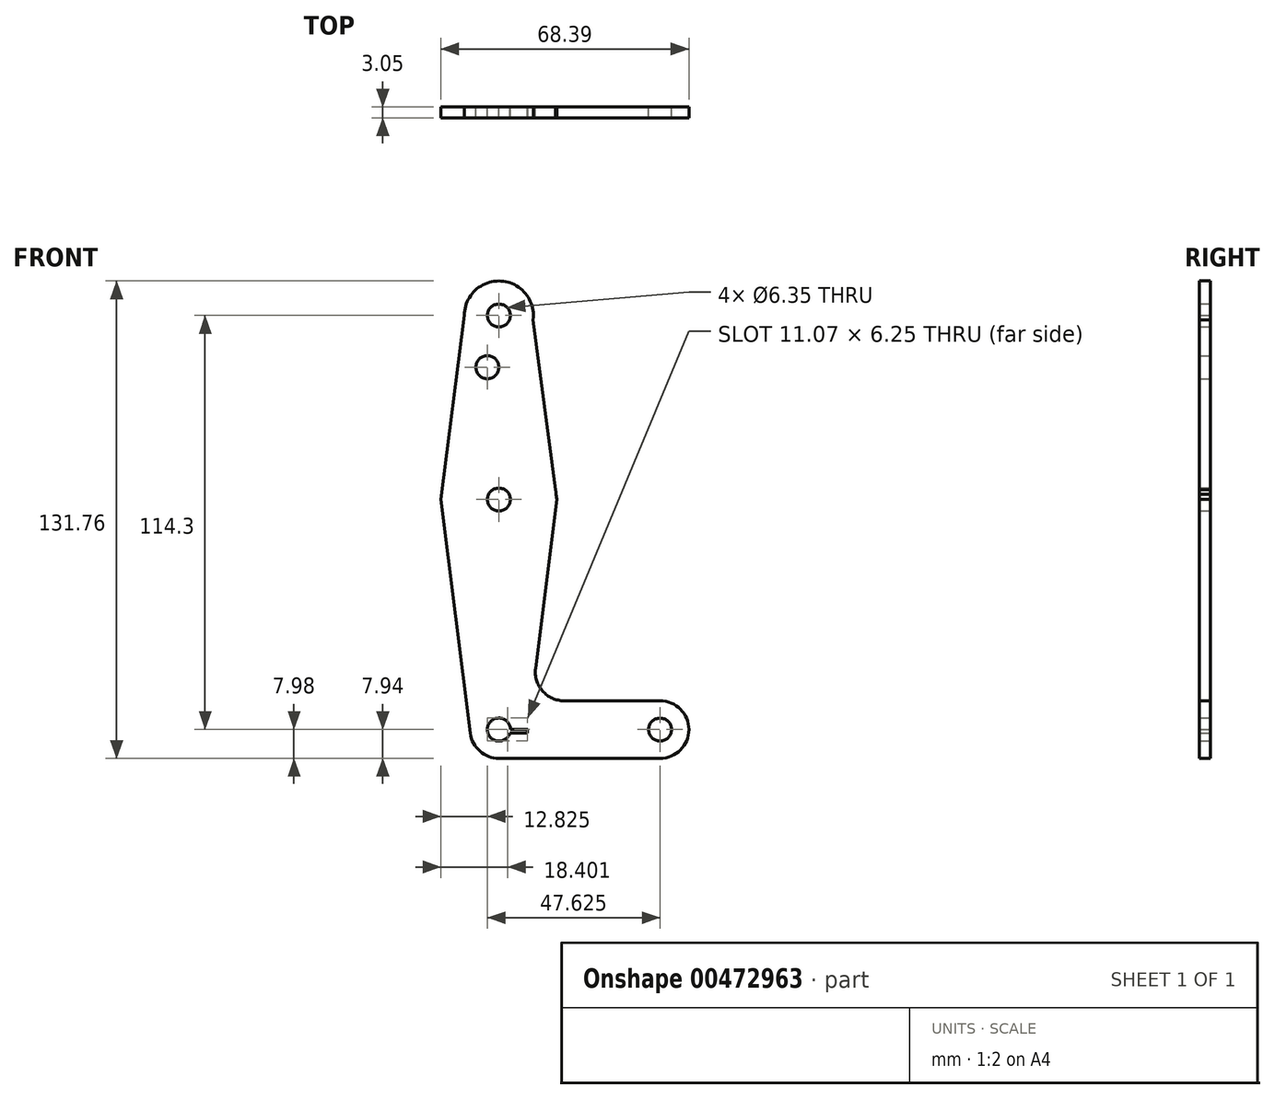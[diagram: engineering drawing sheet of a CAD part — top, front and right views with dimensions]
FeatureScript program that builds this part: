
annotation { "Feature Type Name" : "Feature", "Feature Type Description" : "" }
export const myFeature = defineFeature(function(context is Context, id is Id, definition is map)
    precondition{}
    {
        {
            var Q0;
            Q0=qCreatedBy(makeId("Front.planeOp"),FACE);
            var sketch = newSketch(context, id + "F0", { "sketchPlane" : qUnion([Q0])});
            skLineSegment(sketch, "E0", {"start": v(0, 50.8) * mm, "end": v(0, 0) * mm});
            skLineSegment(sketch, "E1", {"start": v(0, -63.5) * mm, "end": v(0, 0) * mm});
            skLineSegment(sketch, "E2", {"start": v(0, -63.5) * mm, "end": v(44.45, -63.5) * mm});
            skCircle(sketch, "E3", {"center": v(44.45, -63.5) * mm, "radius": 7.94 * mm});
            skCircle(sketch, "E4", {"center": v(0, -63.5) * mm, "radius": 7.94 * mm});
            skCircle(sketch, "E5", {"center": v(0, 0) * mm, "radius": 15.88 * mm});
            skCircle(sketch, "E6", {"center": v(0, 50.8) * mm, "radius": 9.53 * mm});
            skLineSegment(sketch, "E7", {"start": v(-9.53, 50.8) * mm, "end": v(-16, 0) * mm});
            skLineSegment(sketch, "E8", {"start": v(-16, 0) * mm, "end": v(-7.88, -64.5) * mm});
            skLineSegment(sketch, "E9", {"start": v(-7.88, -64.5) * mm, "end": v(7.88, -64.5) * mm});
            skLineSegment(sketch, "E10", {"start": v(10.13, -46.62) * mm, "end": v(16, 0) * mm});
            skLineSegment(sketch, "E11", {"start": v(18.01, -55.56) * mm, "end": v(44.45, -55.56) * mm});
            skLineSegment(sketch, "E12", {"start": v(0, -71.44) * mm, "end": v(44.45, -71.44) * mm});
            skCircle(sketch, "E13", {"center": v(0, 50.8) * mm, "radius": 3.18 * mm});
            skCircle(sketch, "E14", {"center": v(0, 0) * mm, "radius": 3.18 * mm});
            skCircle(sketch, "E15", {"center": v(0, -63.5) * mm, "radius": 3.18 * mm});
            skCircle(sketch, "E16", {"center": v(44.45, -63.5) * mm, "radius": 3.18 * mm});
            skCircle(sketch, "E17", {"center": v(-3.17, 36.53) * mm, "radius": 3.18 * mm});
            skLineSegment(sketch, "E18", {"start": v(9.45, 49.63) * mm, "end": v(16, 0) * mm});
            skArc(sketch, "E19.filletArc", {"start": v(10.13, -46.62) * mm, "mid": v(12.05, -52.87) * mm, "end": v(18.01, -55.56) * mm});
            skSolve(sketch);
        }
        {
            var Q0;
            Q0 = qSketchRegion(id + "F0", true);
            var Q1;
            {var subQ3=sQuery(id+"F0.wireOp",EDGE,"E15");var subQ5=sQuery(id+"F0.wireOp",EDGE,"E2");var subQ6=makeQuery(id+"F0.imprint","INTERSECT",VERTEX,{"derivedFrom":[subQ5,subQ3]});Q1=makeQuery(id+"F0.imprint","IMPRINT",FACE,{"disambiguationData":[TD([[makeQuery(id+"F0.imprint","IMPRINT",EDGE,{"disambiguationData":[TD([[subQ6,-1.0]])],"derivedFrom":subQ5}),1.0]])]});}
            extrude(context, id + "F1", {"entities" : qUnion([Q0, Q1]), "depth" : 3.05 * mm});
        }
    });
